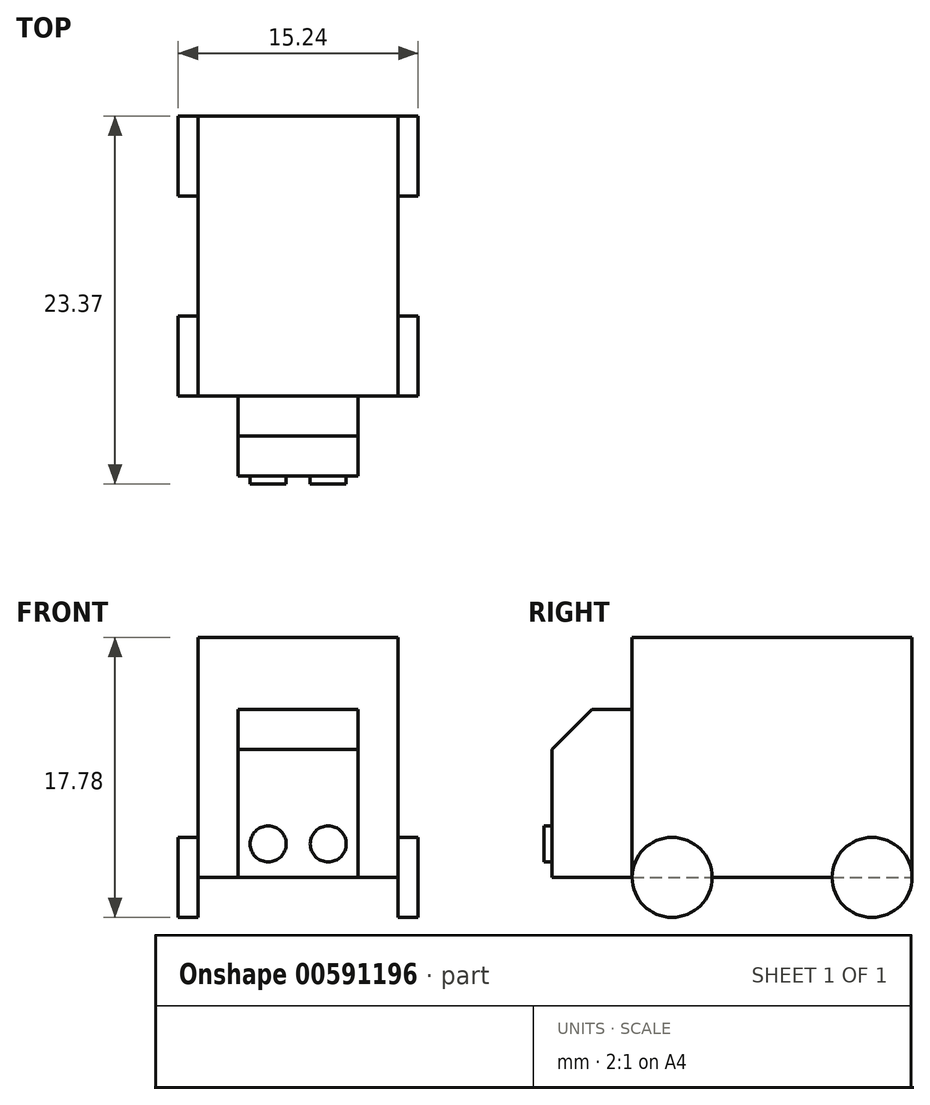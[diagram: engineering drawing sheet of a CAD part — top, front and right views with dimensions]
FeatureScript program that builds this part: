
annotation { "Feature Type Name" : "Feature", "Feature Type Description" : "" }
export const myFeature = defineFeature(function(context is Context, id is Id, definition is map)
    precondition{}
    {
        {
            var Q0;
            Q0=qCreatedBy(makeId("Front.planeOp"),FACE);
            var sketch = newSketch(context, id + "F0", { "sketchPlane" : qUnion([Q0])});
            skLineSegment(sketch, "E0.bottom", {"start": v(6.35, 7.62) * mm, "end": v(-6.35, 7.62) * mm});
            skLineSegment(sketch, "E0.top", {"start": v(6.35, -7.62) * mm, "end": v(-6.35, -7.62) * mm});
            skLineSegment(sketch, "E0.left", {"start": v(6.35, 7.62) * mm, "end": v(6.35, -7.62) * mm});
            skLineSegment(sketch, "E0.right", {"start": v(-6.35, 7.62) * mm, "end": v(-6.35, -7.62) * mm});
            skPoint(sketch, "E0.middle", {"position": v(0, 0) * mm});
            skSolve(sketch);
        }
        {
            var Q0;
            Q0=makeQuery(id+"F0.imprint","IMPRINT",FACE,{"disambiguationData":[TD([[makeQuery(id+"F0.imprint","IMPRINT",EDGE,{"derivedFrom":sQuery(id+"F0.wireOp",EDGE,"E0.bottom")}),1.0]])]});
            extrude(context, id + "F1", {"entities" : qUnion([Q0]), "depth" : 17.78 * mm, "offsetDistance" : 25.4 * mm});
        }
        {
            var Q0;
            Q0=makeQuery(id+"F1.opExtrude","CAP_FACE",FACE,{"disambiguationData":[OSD([sQuery(id+"F0.wireOp",EDGE,"E0.bottom"),sQuery(id+"F0.wireOp",EDGE,"E0.top"),sQuery(id+"F0.wireOp",EDGE,"E0.left"),sQuery(id+"F0.wireOp",EDGE,"E0.right")])],"isStart":false});
            var sketch = newSketch(context, id + "F2", { "sketchPlane" : qUnion([Q0])});
            skLineSegment(sketch, "E1", {"start": v(-3.81, 3.05) * mm, "end": v(3.8, 3.05) * mm});
            skLineSegment(sketch, "E2.bottom", {"start": v(-3.81, 3.05) * mm, "end": v(3.82, 3.05) * mm});
            skLineSegment(sketch, "E2.top", {"start": v(-3.81, -7.62) * mm, "end": v(3.82, -7.62) * mm});
            skLineSegment(sketch, "E3.left", {"start": v(-3.81, 3.05) * mm, "end": v(-3.81, -7.62) * mm});
            skLineSegment(sketch, "E3.right", {"start": v(3.82, 3.05) * mm, "end": v(3.82, -7.62) * mm});
            skSolve(sketch);
        }
        {
            var Q0;
            Q0=makeQuery(id+"F2.imprint","IMPRINT",FACE,{"disambiguationData":[TD([[makeQuery(id+"F2.imprint","IMPRINT",EDGE,{"derivedFrom":sQuery(id+"F2.wireOp",EDGE,"E2.top")}),-1.0]])]});
            extrude(context, id + "F3", {"entities" : qUnion([Q0]), "operationType" : NewBodyOperationType.ADD, "depth" : 5.08 * mm, "offsetDistance" : 25.4 * mm});
        }
        {
            var Q0;
            Q0=makeQuery(id+"F1.opExtrude","SWEPT_FACE",FACE,{"disambiguationData":[OSD([sQuery(id+"F0.wireOp",EDGE,"E0.right")])]});
            var sketch = newSketch(context, id + "F4", { "sketchPlane" : qUnion([Q0])});
            skCircle(sketch, "E4", {"center": v(15.24, -7.62) * mm, "radius": 2.54 * mm});
            skCircle(sketch, "E5", {"center": v(2.54, -7.62) * mm, "radius": 2.54 * mm});
            skSolve(sketch);
        }
        {
            var Q0;
            {var subQ0=sQuery(id+"F4.wireOp",EDGE,"E5");var subQ1=sQuery(id+"F0.wireOp",EDGE,"E0.right");var subQ2=makeQuery(id+"F1.opExtrude","SWEPT_EDGE",EDGE,{"disambiguationData":[OSD([sQuery(id+"F0.wireOp",EDGE,"E0.top"),subQ1])]});var subQ4=makeQuery(id+"F4.imprint","INTERSECT",VERTEX,{"derivedFrom":[subQ2,subQ0]});Q0=makeQuery(id+"F4.imprint","IMPRINT",FACE,{"disambiguationData":[TD([[makeQuery(id+"F4.imprint","IMPRINT",EDGE,{"disambiguationData":[TD([[subQ4,1.0]])],"derivedFrom":subQ0}),1.0]])]});}
            var Q1;
            {var subQ0=sQuery(id+"F4.wireOp",EDGE,"E5");var subQ1=sQuery(id+"F0.wireOp",EDGE,"E0.right");var subQ2=makeQuery(id+"F1.opExtrude","SWEPT_EDGE",EDGE,{"disambiguationData":[OSD([sQuery(id+"F0.wireOp",EDGE,"E0.top"),subQ1])]});var subQ4=makeQuery(id+"F4.imprint","INTERSECT",VERTEX,{"derivedFrom":[subQ2,subQ0]});Q1=makeQuery(id+"F4.imprint","IMPRINT",FACE,{"disambiguationData":[TD([[makeQuery(id+"F4.imprint","IMPRINT",EDGE,{"disambiguationData":[TD([[subQ4,-1.0]])],"derivedFrom":subQ0}),1.0]])]});}
            var Q2;
            {var subQ0=sQuery(id+"F4.wireOp",EDGE,"E4");var subQ1=sQuery(id+"F0.wireOp",EDGE,"E0.right");var subQ2=makeQuery(id+"F1.opExtrude","SWEPT_EDGE",EDGE,{"disambiguationData":[OSD([sQuery(id+"F0.wireOp",EDGE,"E0.top"),subQ1])]});var subQ4=makeQuery(id+"F4.imprint","INTERSECT",VERTEX,{"derivedFrom":[subQ2,subQ0]});Q2=makeQuery(id+"F4.imprint","IMPRINT",FACE,{"disambiguationData":[TD([[makeQuery(id+"F4.imprint","IMPRINT",EDGE,{"disambiguationData":[TD([[subQ4,1.0]])],"derivedFrom":subQ0}),1.0]])]});}
            var Q3;
            {var subQ0=sQuery(id+"F4.wireOp",EDGE,"E4");var subQ1=sQuery(id+"F0.wireOp",EDGE,"E0.right");var subQ2=makeQuery(id+"F1.opExtrude","SWEPT_EDGE",EDGE,{"disambiguationData":[OSD([sQuery(id+"F0.wireOp",EDGE,"E0.top"),subQ1])]});var subQ4=makeQuery(id+"F4.imprint","INTERSECT",VERTEX,{"derivedFrom":[subQ2,subQ0]});Q3=makeQuery(id+"F4.imprint","IMPRINT",FACE,{"disambiguationData":[TD([[makeQuery(id+"F4.imprint","IMPRINT",EDGE,{"disambiguationData":[TD([[subQ4,-1.0]])],"derivedFrom":subQ0}),1.0]])]});}
            extrude(context, id + "F5", {"entities" : qUnion([Q0, Q1, Q2, Q3]), "operationType" : NewBodyOperationType.ADD, "depth" : 1.27 * mm, "offsetDistance" : 25.4 * mm});
        }
        {
            var Q0;
            Q0=makeQuery(id+"F3.opExtrude","CAP_FACE",FACE,{"disambiguationData":[OSD([sQuery(id+"F2.wireOp",EDGE,"E2.bottom"),sQuery(id+"F2.wireOp",EDGE,"E2.top"),sQuery(id+"F2.wireOp",EDGE,"E3.left"),sQuery(id+"F2.wireOp",EDGE,"E3.right")])],"isStart":false});
            var sketch = newSketch(context, id + "F6", { "sketchPlane" : qUnion([Q0])});
            skLineSegment(sketch, "E6", {"start": v(0, 3.05) * mm, "end": v(0, -7.62) * mm});
            skLineSegment(sketch, "E7", {"start": v(0, -5.5) * mm, "end": v(3.82, -5.5) * mm});
            skPoint(sketch, "E8", {"position": v(1.91, -5.5) * mm});
            skLineSegment(sketch, "E9", {"start": v(0, -5.5) * mm, "end": v(-3.81, -5.5) * mm});
            skPoint(sketch, "E10", {"position": v(-1.9, -5.5) * mm});
            skCircle(sketch, "E11", {"center": v(-1.9, -5.5) * mm, "radius": 1.14 * mm});
            skCircle(sketch, "E12", {"center": v(1.91, -5.5) * mm, "radius": 1.14 * mm});
            skSolve(sketch);
        }
        {
            var Q0;
            {var subQ0=sQuery(id+"F6.wireOp",EDGE,"E11");var subQ1=sQuery(id+"F6.wireOp",EDGE,"E9");var subQ2=makeQuery(id+"F6.imprint","INTERSECT",VERTEX,{"disambiguationData":[OD(0.0)],"derivedFrom":[subQ1,subQ0]});Q0=makeQuery(id+"F6.imprint","IMPRINT",FACE,{"disambiguationData":[TD([[makeQuery(id+"F6.imprint","IMPRINT",EDGE,{"disambiguationData":[TD([[subQ2,-1.0]])],"derivedFrom":subQ1}),-1.0]])]});}
            var Q1;
            {var subQ0=sQuery(id+"F6.wireOp",EDGE,"E11");var subQ1=sQuery(id+"F6.wireOp",EDGE,"E9");var subQ2=makeQuery(id+"F6.imprint","INTERSECT",VERTEX,{"disambiguationData":[OD(0.0)],"derivedFrom":[subQ1,subQ0]});Q1=makeQuery(id+"F6.imprint","IMPRINT",FACE,{"disambiguationData":[TD([[makeQuery(id+"F6.imprint","IMPRINT",EDGE,{"disambiguationData":[TD([[subQ2,-1.0]])],"derivedFrom":subQ1}),1.0]])]});}
            var Q2;
            {var subQ0=sQuery(id+"F6.wireOp",EDGE,"E12");var subQ1=sQuery(id+"F6.wireOp",EDGE,"E7");var subQ2=makeQuery(id+"F6.imprint","INTERSECT",VERTEX,{"disambiguationData":[OD(0.0)],"derivedFrom":[subQ1,subQ0]});Q2=makeQuery(id+"F6.imprint","IMPRINT",FACE,{"disambiguationData":[TD([[makeQuery(id+"F6.imprint","IMPRINT",EDGE,{"disambiguationData":[TD([[subQ2,-1.0]])],"derivedFrom":subQ1}),1.0]])]});}
            var Q3;
            {var subQ0=sQuery(id+"F6.wireOp",EDGE,"E12");var subQ1=sQuery(id+"F6.wireOp",EDGE,"E7");var subQ2=makeQuery(id+"F6.imprint","INTERSECT",VERTEX,{"disambiguationData":[OD(0.0)],"derivedFrom":[subQ1,subQ0]});Q3=makeQuery(id+"F6.imprint","IMPRINT",FACE,{"disambiguationData":[TD([[makeQuery(id+"F6.imprint","IMPRINT",EDGE,{"disambiguationData":[TD([[subQ2,-1.0]])],"derivedFrom":subQ1}),-1.0]])]});}
            extrude(context, id + "F7", {"entities" : qUnion([Q0, Q1, Q2, Q3]), "operationType" : NewBodyOperationType.ADD, "depth" : 0.5 * mm, "offsetDistance" : 25.4 * mm});
        }
        {
            var Q0;
            Q0=makeQuery(id+"F1.opExtrude","SWEPT_FACE",FACE,{"disambiguationData":[OSD([sQuery(id+"F0.wireOp",EDGE,"E0.left")])]});
            var sketch = newSketch(context, id + "F8", { "sketchPlane" : qUnion([Q0])});
            skCircle(sketch, "E13", {"center": v(-15.24, -7.62) * mm, "radius": 2.54 * mm});
            skCircle(sketch, "E14", {"center": v(-2.54, -7.62) * mm, "radius": 2.54 * mm});
            skSolve(sketch);
        }
        {
            var Q0;
            {var subQ0=sQuery(id+"F8.wireOp",EDGE,"E13");var subQ1=sQuery(id+"F0.wireOp",EDGE,"E0.left");var subQ2=makeQuery(id+"F1.opExtrude","SWEPT_EDGE",EDGE,{"disambiguationData":[OSD([sQuery(id+"F0.wireOp",EDGE,"E0.top"),subQ1])]});var subQ4=makeQuery(id+"F8.imprint","INTERSECT",VERTEX,{"derivedFrom":[subQ2,subQ0]});Q0=makeQuery(id+"F8.imprint","IMPRINT",FACE,{"disambiguationData":[TD([[makeQuery(id+"F8.imprint","IMPRINT",EDGE,{"disambiguationData":[TD([[subQ4,-1.0]])],"derivedFrom":subQ0}),1.0]])]});}
            var Q1;
            {var subQ0=sQuery(id+"F8.wireOp",EDGE,"E13");var subQ1=sQuery(id+"F0.wireOp",EDGE,"E0.left");var subQ2=makeQuery(id+"F1.opExtrude","SWEPT_EDGE",EDGE,{"disambiguationData":[OSD([sQuery(id+"F0.wireOp",EDGE,"E0.top"),subQ1])]});var subQ4=makeQuery(id+"F8.imprint","INTERSECT",VERTEX,{"derivedFrom":[subQ2,subQ0]});Q1=makeQuery(id+"F8.imprint","IMPRINT",FACE,{"disambiguationData":[TD([[makeQuery(id+"F8.imprint","IMPRINT",EDGE,{"disambiguationData":[TD([[subQ4,1.0]])],"derivedFrom":subQ0}),1.0]])]});}
            var Q2;
            {var subQ0=sQuery(id+"F8.wireOp",EDGE,"E14");var subQ1=sQuery(id+"F0.wireOp",EDGE,"E0.left");var subQ2=makeQuery(id+"F1.opExtrude","SWEPT_EDGE",EDGE,{"disambiguationData":[OSD([sQuery(id+"F0.wireOp",EDGE,"E0.top"),subQ1])]});var subQ4=makeQuery(id+"F8.imprint","INTERSECT",VERTEX,{"derivedFrom":[subQ2,subQ0]});Q2=makeQuery(id+"F8.imprint","IMPRINT",FACE,{"disambiguationData":[TD([[makeQuery(id+"F8.imprint","IMPRINT",EDGE,{"disambiguationData":[TD([[subQ4,1.0]])],"derivedFrom":subQ0}),1.0]])]});}
            var Q3;
            {var subQ0=sQuery(id+"F8.wireOp",EDGE,"E14");var subQ1=sQuery(id+"F0.wireOp",EDGE,"E0.left");var subQ2=makeQuery(id+"F1.opExtrude","SWEPT_EDGE",EDGE,{"disambiguationData":[OSD([sQuery(id+"F0.wireOp",EDGE,"E0.top"),subQ1])]});var subQ4=makeQuery(id+"F8.imprint","INTERSECT",VERTEX,{"derivedFrom":[subQ2,subQ0]});Q3=makeQuery(id+"F8.imprint","IMPRINT",FACE,{"disambiguationData":[TD([[makeQuery(id+"F8.imprint","IMPRINT",EDGE,{"disambiguationData":[TD([[subQ4,-1.0]])],"derivedFrom":subQ0}),1.0]])]});}
            extrude(context, id + "F9", {"entities" : qUnion([Q0, Q1, Q2, Q3]), "operationType" : NewBodyOperationType.ADD, "depth" : 1.27 * mm, "offsetDistance" : 25.4 * mm});
        }
        {
            var Q0;
            Q0=makeQuery(id+"F3.opExtrude","CAP_EDGE",EDGE,{"disambiguationData":[OSD([sQuery(id+"F2.wireOp",EDGE,"E2.bottom")])],"isStart":false});
            chamfer(context, id + "F10", {"entities" : qUnion([Q0]), "width" : 2.54 * mm, "tangentPropagation" : true});
        }
    });
